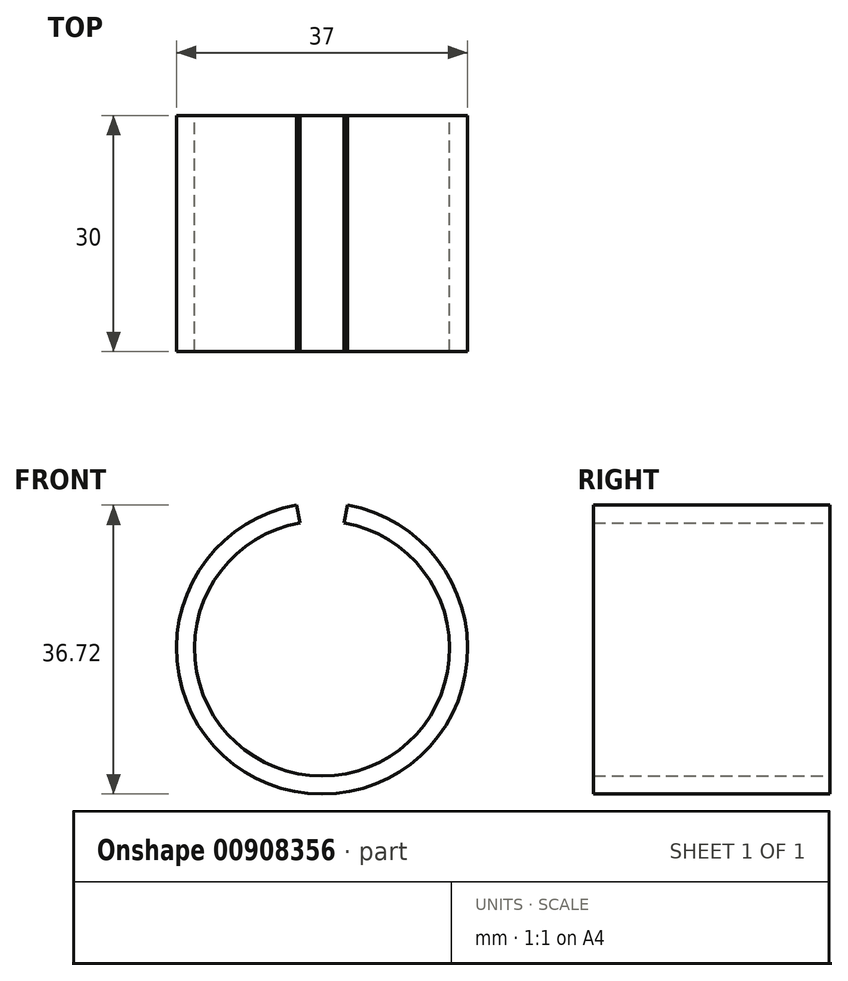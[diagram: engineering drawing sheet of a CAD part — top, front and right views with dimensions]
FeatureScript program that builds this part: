
annotation { "Feature Type Name" : "Feature", "Feature Type Description" : "" }
export const myFeature = defineFeature(function(context is Context, id is Id, definition is map)
    precondition{}
    {
        {
            var Q0;
            Q0=qCreatedBy(makeId("Front.planeOp"),FACE);
            var sketch = newSketch(context, id + "F0", { "sketchPlane" : qUnion([Q0])});
            skArc(sketch, "E0", {"start": v(-2.81, 15.95) * mm, "mid": v(0, -16.2) * mm, "end": v(2.81, 15.95) * mm});
            skArc(sketch, "E1", {"start": v(-3.21, 18.22) * mm, "mid": v(0, -18.5) * mm, "end": v(3.21, 18.22) * mm});
            skLineSegment(sketch, "E2", {"start": v(2.81, 15.95) * mm, "end": v(3.21, 18.22) * mm});
            skLineSegment(sketch, "E3", {"start": v(-2.81, 15.95) * mm, "end": v(-3.21, 18.22) * mm});
            skSolve(sketch);
        }
        {
            var Q0;
            Q0=makeQuery(id+"F0.imprint","IMPRINT",FACE,{"disambiguationData":[TD([[makeQuery(id+"F0.imprint","IMPRINT",EDGE,{"derivedFrom":sQuery(id+"F0.wireOp",EDGE,"E0")}),-1.0]])]});
            extrude(context, id + "F1", {"entities" : qUnion([Q0]), "depth" : 30 * mm, "offsetDistance" : 25 * mm});
        }
    });
